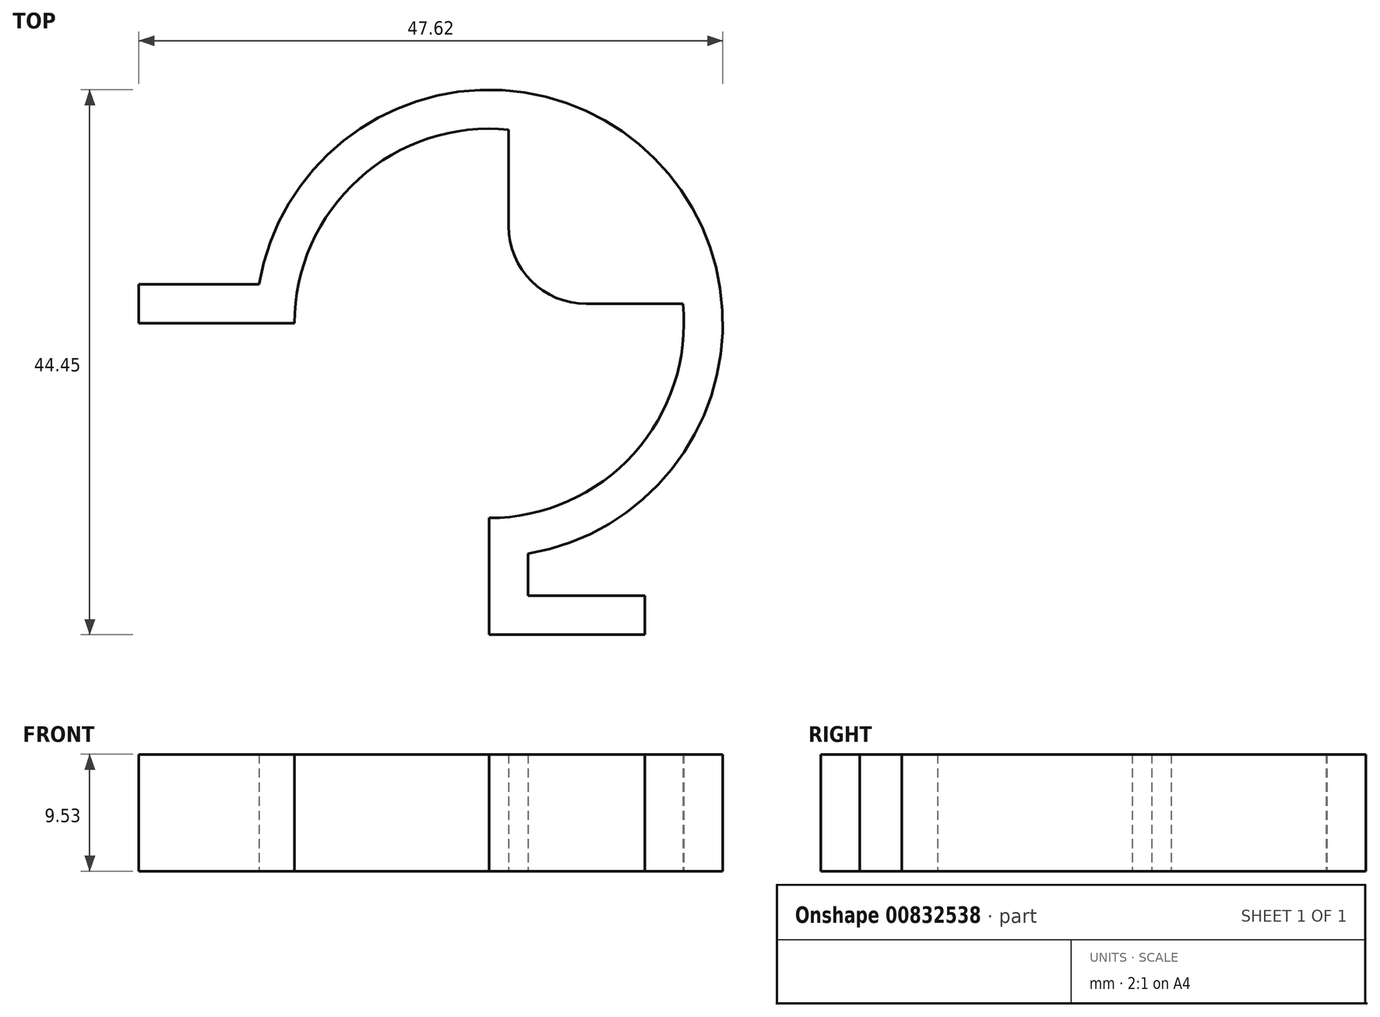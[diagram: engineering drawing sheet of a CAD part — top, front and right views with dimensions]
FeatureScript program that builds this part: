
annotation { "Feature Type Name" : "Feature", "Feature Type Description" : "" }
export const myFeature = defineFeature(function(context is Context, id is Id, definition is map)
    precondition{}
    {
        {
            var Q0;
            Q0=qCreatedBy(makeId("Top.planeOp"),FACE);
            var sketch = newSketch(context, id + "F0", { "sketchPlane" : qUnion([Q0])});
            skArc(sketch, "E0", {"start": v(0, -15.88) * mm, "mid": v(11.77, -10.65) * mm, "end": v(15.8, 1.59) * mm});
            skArc(sketch, "E1", {"start": v(3.18, -18.78) * mm, "mid": v(13.47, 13.47) * mm, "end": v(-18.78, 3.18) * mm});
            skLineSegment(sketch, "E2", {"start": v(0, -15.88) * mm, "end": v(0, -25.4) * mm});
            skLineSegment(sketch, "E3", {"start": v(0, -25.4) * mm, "end": v(12.7, -25.4) * mm});
            skLineSegment(sketch, "E4", {"start": v(12.7, -25.4) * mm, "end": v(12.7, -22.22) * mm});
            skLineSegment(sketch, "E5", {"start": v(12.7, -22.22) * mm, "end": v(3.18, -22.22) * mm});
            skLineSegment(sketch, "E6", {"start": v(3.18, -22.22) * mm, "end": v(3.18, -18.78) * mm});
            skLineSegment(sketch, "E7", {"start": v(-15.88, 0) * mm, "end": v(-28.58, 0) * mm});
            skLineSegment(sketch, "E8", {"start": v(-28.58, 0) * mm, "end": v(-28.58, 3.17) * mm});
            skLineSegment(sketch, "E9", {"start": v(-28.58, 3.17) * mm, "end": v(-18.78, 3.17) * mm});
            skLineSegment(sketch, "E10.0", {"start": v(7.94, 1.59) * mm, "end": v(15.8, 1.59) * mm});
            skLineSegment(sketch, "E10.1", {"start": v(1.59, 15.8) * mm, "end": v(1.59, 7.94) * mm});
            skArc(sketch, "E11.trimOffspring", {"start": v(1.59, 15.8) * mm, "mid": v(-10.65, 11.77) * mm, "end": v(-15.88, 0) * mm});
            skPoint(sketch, "E12.visualSharp", {"position": v(1.59, 1.59) * mm});
            skArc(sketch, "E12.filletArc", {"start": v(1.59, 7.94) * mm, "mid": v(3.45, 3.45) * mm, "end": v(7.94, 1.59) * mm});
            skSolve(sketch);
        }
        {
            var Q0;
            Q0=makeQuery(id+"F0.imprint","IMPRINT",FACE,{"disambiguationData":[TD([[makeQuery(id+"F0.imprint","IMPRINT",EDGE,{"derivedFrom":sQuery(id+"F0.wireOp",EDGE,"E0")}),-1.0]])]});
            extrude(context, id + "F1", {"entities" : qUnion([Q0]), "depth" : 9.52 * mm, "offsetDistance" : 25.4 * mm});
        }
    });
